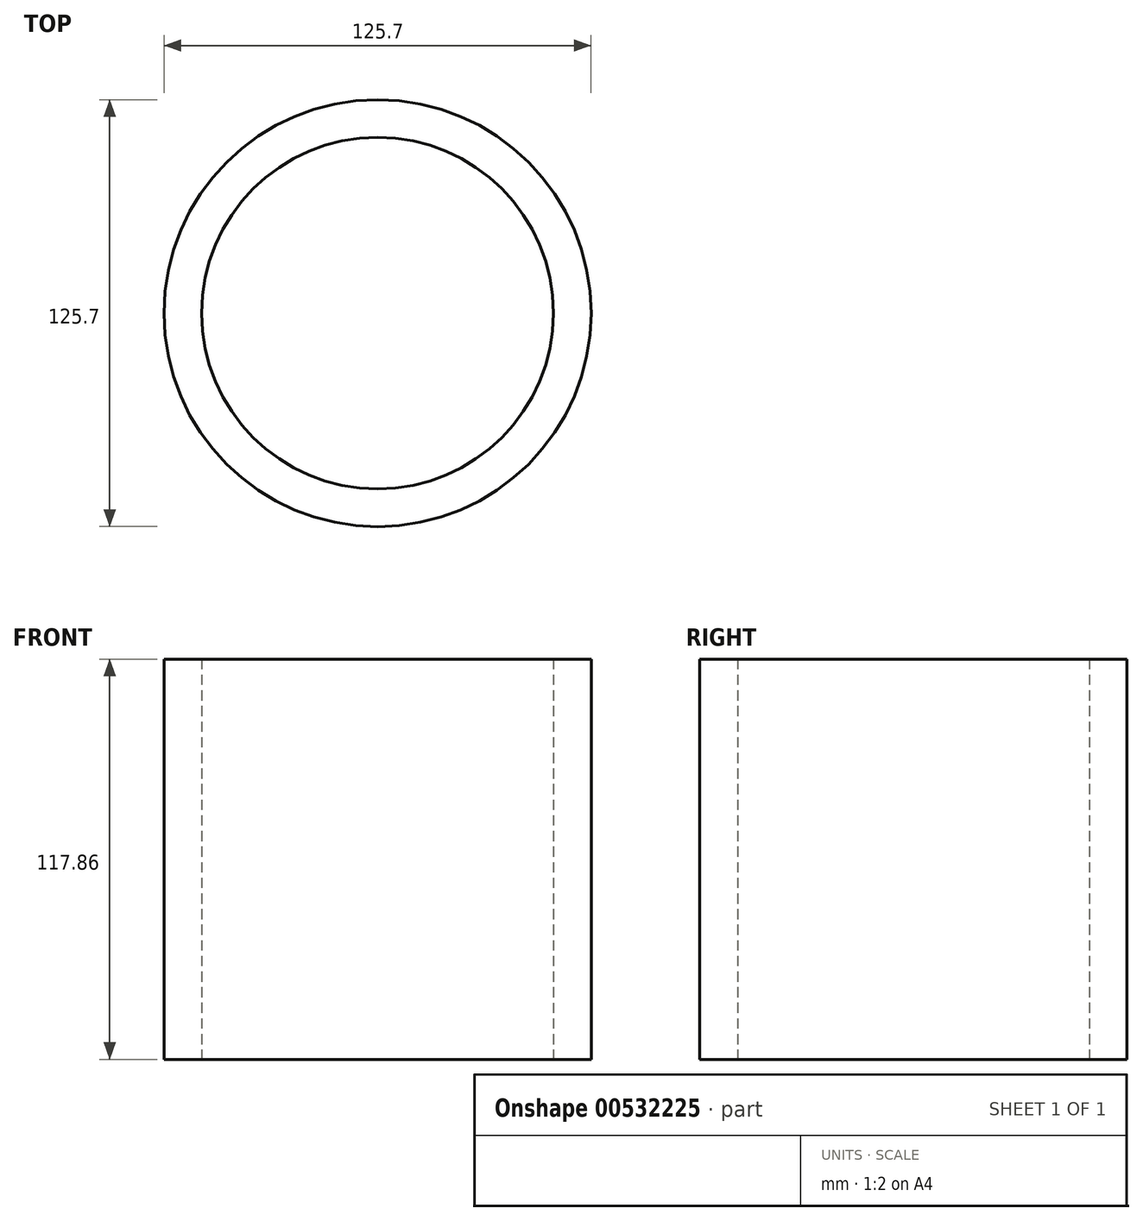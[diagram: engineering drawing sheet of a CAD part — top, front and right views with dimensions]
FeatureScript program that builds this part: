
annotation { "Feature Type Name" : "Feature", "Feature Type Description" : "" }
export const myFeature = defineFeature(function(context is Context, id is Id, definition is map)
    precondition{}
    {
        {
            var Q0;
            Q0=qCreatedBy(makeId("Top.planeOp"),FACE);
            var sketch = newSketch(context, id + "F0", { "sketchPlane" : qUnion([Q0])});
            skCircle(sketch, "E0", {"center": v(0, 0) * mm, "radius": 62.85 * mm});
            skCircle(sketch, "E1", {"center": v(0, 0) * mm, "radius": 51.74 * mm});
            skSolve(sketch);
        }
        {
            var Q0;
            Q0 = qSketchRegion(id + "F0", true);
            extrude(context, id + "F1", {"entities" : qUnion([Q0]), "depth" : 117.86 * mm, "offsetDistance" : 25.4 * mm});
        }
    });
